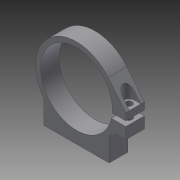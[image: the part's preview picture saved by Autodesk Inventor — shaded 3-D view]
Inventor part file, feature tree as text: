
AUTODESK INVENTOR PART (.ipt)
format: ipt  version: 2014 SP1 (Build 180222100, 222)  size: 154,624 bytes
history: native  units: in
note: dims shown in document units (in); Inventor stores cm internally (conversion verified against a paired STEP export)
features: extrude x5, sketch x5, thread x3
ambient origin geometry x8: Origin, YZ Plane, XZ Plane, XY Plane, X Axis, Y Axis, Z Axis, Center Point
bodies: Solid1 (feature_tree)
feature tree (13):
  extrude  "Extrusion1"  Depth=1.65in
  extrude  "Extrusion2"  Depth=0.375in
  thread  "Thread1"  [1 undecoded]
  thread  "Thread2"  [1 undecoded]
  extrude  "Extrusion3"  Depth=0.375in TaperAngle=0.0deg
  extrude  "Extrusion4"  Depth=0.125in
  extrude  "Extrusion5"  Depth=0.375in TaperAngle=0.0deg
  thread  "Thread3"  [1 undecoded]
  sketch  "Sketch1"  dims[d0=1.45in d1=1.65in]
  sketch  "Sketch2"  dims[d9=0.375in d10=0.0in d12=1.061in d13=0.138in d14=0.138in]
  sketch  "Sketch3"  dims[d15=0.375in d16=0.0in d17=1.0in d18=0.0in]
  sketch  "Sketch4"  dims[d19=1.0in d20=0.0in d21=0.125in]
  sketch  "Sketch5"  dims[d22=0.138in d23=1.0in d24=0.0in d26=0.4in d27=0.23in d28=0.125in d29=0.0in d30=0.375in d31=0.0in d32=1.0in d33=0.0in]
note: 3 required parameter values undecoded (feature->parameter linkage not recoverable at this tier; creation-order binding heuristic only, values carry confidence <= 0.55)
